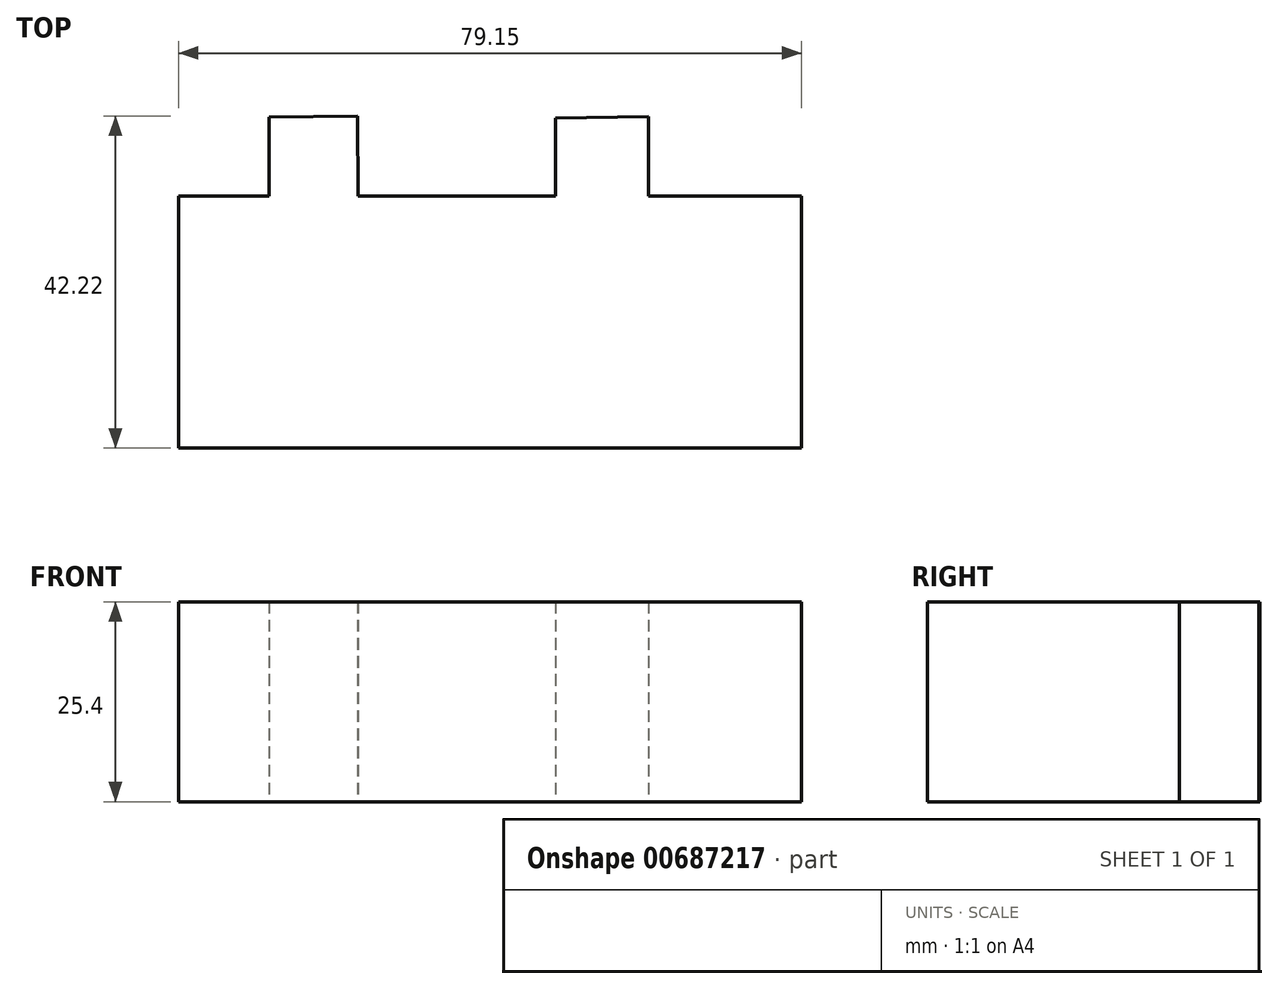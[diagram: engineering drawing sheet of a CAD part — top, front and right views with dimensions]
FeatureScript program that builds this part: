
annotation { "Feature Type Name" : "Feature", "Feature Type Description" : "" }
export const myFeature = defineFeature(function(context is Context, id is Id, definition is map)
    precondition{}
    {
        {
            var Q0;
            Q0=qCreatedBy(makeId("Top.planeOp"),FACE);
            var sketch = newSketch(context, id + "F0", { "sketchPlane" : qUnion([Q0])});
            skLineSegment(sketch, "E0.bottom", {"start": v(-40.83, 32) * mm, "end": v(38.32, 32) * mm});
            skLineSegment(sketch, "E0.top", {"start": v(-40.83, 0) * mm, "end": v(38.32, 0) * mm});
            skLineSegment(sketch, "E0.left", {"start": v(-40.83, 32) * mm, "end": v(-40.83, 0) * mm});
            skLineSegment(sketch, "E0.right", {"start": v(38.32, 32) * mm, "end": v(38.32, 0) * mm});
            skLineSegment(sketch, "E1", {"start": v(-29.33, 32) * mm, "end": v(-29.33, 42.03) * mm});
            skLineSegment(sketch, "E2", {"start": v(-29.33, 42.03) * mm, "end": v(-18.07, 42.22) * mm});
            skLineSegment(sketch, "E3", {"start": v(-18.07, 42.22) * mm, "end": v(-17.97, 32) * mm});
            skLineSegment(sketch, "E4", {"start": v(-17.97, 32) * mm, "end": v(-17.97, 32) * mm});
            skLineSegment(sketch, "E5", {"start": v(7.07, 32) * mm, "end": v(7.07, 41.96) * mm});
            skLineSegment(sketch, "E6", {"start": v(7.07, 41.96) * mm, "end": v(18.87, 42.12) * mm});
            skLineSegment(sketch, "E7", {"start": v(18.87, 42.12) * mm, "end": v(18.87, 32) * mm});
            skLineSegment(sketch, "E8", {"start": v(-8.66, 32) * mm, "end": v(-8.66, 18.87) * mm});
            skLineSegment(sketch, "E9", {"start": v(-8.66, 18.87) * mm, "end": v(-13.44, 18.87) * mm});
            skLineSegment(sketch, "E10", {"start": v(-13.44, 18.87) * mm, "end": v(-13.44, 13.28) * mm});
            skLineSegment(sketch, "E11", {"start": v(-13.44, 13.28) * mm, "end": v(-8.66, 13.28) * mm});
            skLineSegment(sketch, "E12", {"start": v(-8.66, 13.28) * mm, "end": v(-8.66, 7.3) * mm});
            skLineSegment(sketch, "E13", {"start": v(-8.66, 7.3) * mm, "end": v(0, 7.3) * mm});
            skLineSegment(sketch, "E14", {"start": v(0, 7.3) * mm, "end": v(0, 13.13) * mm});
            skLineSegment(sketch, "E15", {"start": v(0, 13.13) * mm, "end": v(4.93, 13.13) * mm});
            skLineSegment(sketch, "E16", {"start": v(4.93, 13.13) * mm, "end": v(5.17, 18.46) * mm});
            skLineSegment(sketch, "E17", {"start": v(5.17, 18.46) * mm, "end": v(0, 18.46) * mm});
            skLineSegment(sketch, "E18", {"start": v(0, 18.46) * mm, "end": v(0, 32) * mm});
            skSolve(sketch);
        }
        {
            var Q0;
            Q0=makeQuery(id+"F0.imprint","IMPRINT",FACE,{"disambiguationData":[TD([[makeQuery(id+"F0.imprint","IMPRINT",EDGE,{"derivedFrom":sQuery(id+"F0.wireOp",EDGE,"E0.top")}),1.0]])]});
            extrude(context, id + "F1", {"entities" : qUnion([Q0]), "depth" : 25.4 * mm, "offsetDistance" : 25.4 * mm});
        }
        {
            var Q0;
            Q0 = qSketchRegion(id + "F0", true);
            extrude(context, id + "F2", {"entities" : qUnion([Q0]), "operationType" : NewBodyOperationType.ADD, "depth" : 25.4 * mm, "offsetDistance" : 25.4 * mm});
        }
    });
